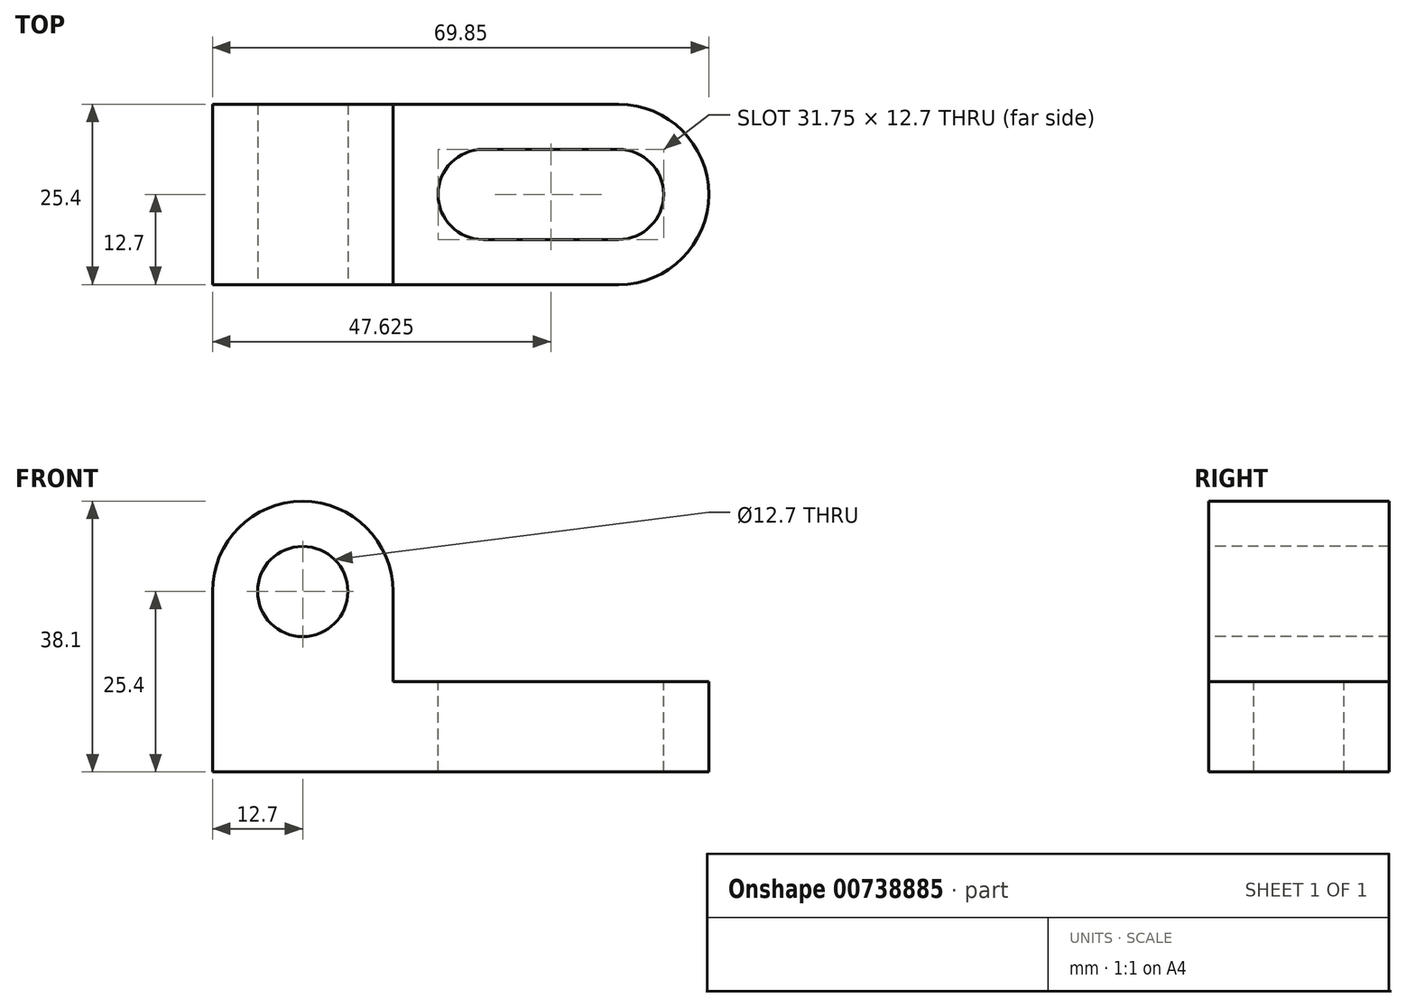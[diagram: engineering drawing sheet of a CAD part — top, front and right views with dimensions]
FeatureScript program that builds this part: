
annotation { "Feature Type Name" : "Feature", "Feature Type Description" : "" }
export const myFeature = defineFeature(function(context is Context, id is Id, definition is map)
    precondition{}
    {
        {
            var Q0;
            Q0=qCreatedBy(makeId("Front.planeOp"),FACE);
            var sketch = newSketch(context, id + "F0", { "sketchPlane" : qUnion([Q0])});
            skLineSegment(sketch, "E0", {"start": v(0, 0) * mm, "end": v(0, 38.1) * mm});
            skLineSegment(sketch, "E1", {"start": v(0, 38.1) * mm, "end": v(69.85, 38.1) * mm});
            skLineSegment(sketch, "E2", {"start": v(69.85, 38.1) * mm, "end": v(69.85, 0) * mm});
            skLineSegment(sketch, "E3", {"start": v(69.85, 0) * mm, "end": v(0, 0) * mm});
            skSolve(sketch);
        }
        {
            var Q0;
            Q0=makeQuery(id+"F0.imprint","IMPRINT",FACE,{"disambiguationData":[TD([[makeQuery(id+"F0.imprint","IMPRINT",EDGE,{"derivedFrom":sQuery(id+"F0.wireOp",EDGE,"E0")}),-1.0]])]});
            extrude(context, id + "F1", {"entities" : qUnion([Q0]), "depth" : 25.4 * mm, "offsetDistance" : 25.4 * mm});
        }
        {
            var Q0;
            Q0=makeQuery(id+"F1.opExtrude","CAP_FACE",FACE,{"disambiguationData":[OSD([sQuery(id+"F0.wireOp",EDGE,"E0"),sQuery(id+"F0.wireOp",EDGE,"E1"),sQuery(id+"F0.wireOp",EDGE,"E2"),sQuery(id+"F0.wireOp",EDGE,"E3")])],"isStart":false});
            var sketch = newSketch(context, id + "F2", { "sketchPlane" : qUnion([Q0])});
            skLineSegment(sketch, "E4", {"start": v(25.4, 38.1) * mm, "end": v(25.4, 12.7) * mm});
            skLineSegment(sketch, "E5", {"start": v(25.4, 12.7) * mm, "end": v(69.85, 12.7) * mm});
            skSolve(sketch);
        }
        {
            var Q0;
            Q0 = qSketchRegion(id + "F2", true);
            var Q1;
            {var subQ0=sQuery(id+"F2.wireOp",EDGE,"E4");Q1=makeQuery(id+"F2.imprint","IMPRINT",FACE,{"disambiguationData":[TD([[makeQuery(id+"F2.imprint","IMPRINT",EDGE,{"derivedFrom":subQ0}),1.0]])]});}
            extrude(context, id + "F3", {"entities" : qUnion([Q0, Q1]), "operationType" : NewBodyOperationType.REMOVE, "oppositeDirection" : true, "depth" : 25.4 * mm, "offsetDistance" : 25.4 * mm});
        }
        {
            var Q0;
            Q0=makeQuery(id+"F1.opExtrude","CAP_FACE",FACE,{"disambiguationData":[OSD([sQuery(id+"F0.wireOp",EDGE,"E0"),sQuery(id+"F0.wireOp",EDGE,"E1"),sQuery(id+"F0.wireOp",EDGE,"E2"),sQuery(id+"F0.wireOp",EDGE,"E3")])],"isStart":false});
            var sketch = newSketch(context, id + "F4", { "sketchPlane" : qUnion([Q0])});
            skCircle(sketch, "E6", {"center": v(12.7, 25.4) * mm, "radius": 6.35 * mm});
            skArc(sketch, "E7", {"start": v(25.4, 25.4) * mm, "mid": v(12.7, 38.1) * mm, "end": v(0, 25.4) * mm});
            skSolve(sketch);
        }
        {
            var Q0;
            Q0 = qSketchRegion(id + "F4", true);
            var Q1;
            {var subQ0=sQuery(id+"F4.wireOp",EDGE,"E7");var subQ1=makeQuery(id+"F1.opExtrude","CAP_EDGE",EDGE,{"disambiguationData":[OSD([sQuery(id+"F0.wireOp",EDGE,"E0")])],"isStart":false});var subQ2=makeQuery(id+"F4.imprint","INTERSECT",VERTEX,{"derivedFrom":[subQ1,subQ0]});Q1=makeQuery(id+"F4.imprint","IMPRINT",FACE,{"disambiguationData":[TD([[makeQuery(id+"F4.imprint","IMPRINT",EDGE,{"disambiguationData":[TD([[subQ2,1.0]])],"derivedFrom":subQ0}),-1.0]])]});}
            var Q2;
            {var subQ0=sQuery(id+"F4.wireOp",EDGE,"E7");var subQ1=makeQuery(id+"F3.boolean.opBoolean","COPY",EDGE,{"derivedFrom":makeQuery(id+"F3.opExtrude","CAP_EDGE",EDGE,{"disambiguationData":[OSD([sQuery(id+"F2.wireOp",EDGE,"E4")])],"isStart":true})});var subQ2=makeQuery(id+"F4.imprint","INTERSECT",VERTEX,{"derivedFrom":[subQ1,subQ0]});Q2=makeQuery(id+"F4.imprint","IMPRINT",FACE,{"disambiguationData":[TD([[makeQuery(id+"F4.imprint","IMPRINT",EDGE,{"disambiguationData":[TD([[subQ2,-1.0]])],"derivedFrom":subQ0}),-1.0]])]});}
            extrude(context, id + "F5", {"entities" : qUnion([Q0, Q1, Q2]), "operationType" : NewBodyOperationType.REMOVE, "oppositeDirection" : true, "depth" : 25.4 * mm, "offsetDistance" : 25.4 * mm});
        }
        {
            var Q0;
            Q0=makeQuery(id+"F3.boolean.opBoolean","COPY",FACE,{"derivedFrom":makeQuery(id+"F3.opExtrude","SWEPT_FACE",FACE,{"disambiguationData":[OSD([sQuery(id+"F2.wireOp",EDGE,"E5")])]})});
            var sketch = newSketch(context, id + "F6", { "sketchPlane" : qUnion([Q0])});
            skCircle(sketch, "E8", {"center": v(38.1, -12.7) * mm, "radius": 6.35 * mm});
            skCircle(sketch, "E9", {"center": v(57.15, -12.7) * mm, "radius": 6.35 * mm});
            skLineSegment(sketch, "E10", {"start": v(38.1, -6.35) * mm, "end": v(57.15, -6.35) * mm});
            skLineSegment(sketch, "E11", {"start": v(57.15, -19.05) * mm, "end": v(38.1, -19.05) * mm});
            skArc(sketch, "E12", {"start": v(57.15, -25.4) * mm, "mid": v(69.85, -12.7) * mm, "end": v(57.15, 0) * mm});
            skSolve(sketch);
        }
        {
            var Q0;
            Q0 = qSketchRegion(id + "F6", true);
            var Q1;
            {var subQ0=sQuery(id+"F6.wireOp",EDGE,"E12");var subQ1=sQuery(id+"F2.wireOp",EDGE,"E5");var subQ2=makeQuery(id+"F3.boolean.opBoolean","COPY",EDGE,{"derivedFrom":makeQuery(id+"F3.opExtrude","CAP_EDGE",EDGE,{"disambiguationData":[OSD([subQ1])],"isStart":false})});var subQ3=makeQuery(id+"F6.imprint","INTERSECT",VERTEX,{"derivedFrom":[subQ2,subQ0]});Q1=makeQuery(id+"F6.imprint","IMPRINT",FACE,{"disambiguationData":[TD([[makeQuery(id+"F6.imprint","IMPRINT",EDGE,{"disambiguationData":[TD([[subQ3,1.0]])],"derivedFrom":subQ0}),-1.0]])]});}
            var Q2;
            {var subQ0=sQuery(id+"F6.wireOp",EDGE,"E12");var subQ1=sQuery(id+"F2.wireOp",EDGE,"E5");var subQ2=makeQuery(id+"F3.boolean.opBoolean","COPY",EDGE,{"derivedFrom":makeQuery(id+"F3.opExtrude","CAP_EDGE",EDGE,{"disambiguationData":[OSD([subQ1])],"isStart":true})});var subQ3=makeQuery(id+"F6.imprint","INTERSECT",VERTEX,{"derivedFrom":[subQ2,subQ0]});Q2=makeQuery(id+"F6.imprint","IMPRINT",FACE,{"disambiguationData":[TD([[makeQuery(id+"F6.imprint","IMPRINT",EDGE,{"disambiguationData":[TD([[subQ3,-1.0]])],"derivedFrom":subQ0}),-1.0]])]});}
            extrude(context, id + "F7", {"entities" : qUnion([Q0, Q1, Q2]), "operationType" : NewBodyOperationType.REMOVE, "oppositeDirection" : true, "depth" : 25.4 * mm, "offsetDistance" : 25.4 * mm});
        }
    });
